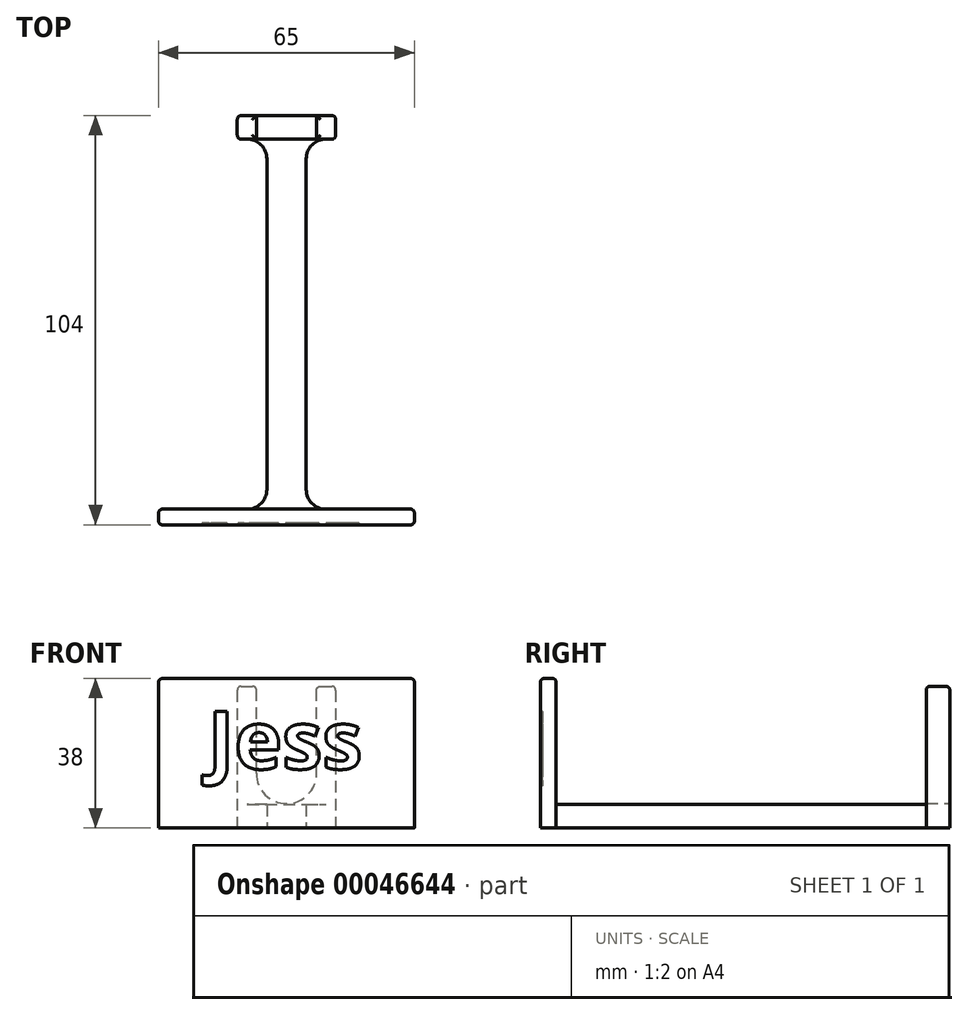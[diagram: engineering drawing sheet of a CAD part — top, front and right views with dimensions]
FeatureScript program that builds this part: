
annotation { "Feature Type Name" : "Feature", "Feature Type Description" : "" }
export const myFeature = defineFeature(function(context is Context, id is Id, definition is map)
    precondition{}
    {
        {
            var Q0;
            Q0=qCreatedBy(makeId("Top.planeOp"),FACE);
            var sketch = newSketch(context, id + "F0", { "sketchPlane" : qUnion([Q0])});
            skLineSegment(sketch, "E0.top", {"start": v(-32.5, -96) * mm, "end": v(32.5, -96) * mm});
            skLineSegment(sketch, "E0.left", {"start": v(-32.5, -92) * mm, "end": v(-32.5, -96) * mm});
            skLineSegment(sketch, "E0.right", {"start": v(32.5, -92) * mm, "end": v(32.5, -96) * mm});
            skLineSegment(sketch, "E1", {"start": v(-5, -92) * mm, "end": v(-5, 2) * mm});
            skLineSegment(sketch, "E2", {"start": v(5, -92) * mm, "end": v(5, 2) * mm});
            skLineSegment(sketch, "E3", {"start": v(32.5, -92) * mm, "end": v(5, -92) * mm});
            skLineSegment(sketch, "E4", {"start": v(-32.5, -92) * mm, "end": v(-5, -92) * mm});
            skLineSegment(sketch, "E5", {"start": v(-12.5, 8) * mm, "end": v(12.5, 8) * mm});
            skLineSegment(sketch, "E6", {"start": v(12.5, 8) * mm, "end": v(12.5, 2) * mm});
            skLineSegment(sketch, "E7", {"start": v(12.5, 2) * mm, "end": v(5, 2) * mm});
            skLineSegment(sketch, "E8", {"start": v(-12.5, 8) * mm, "end": v(-12.5, 2) * mm});
            skLineSegment(sketch, "E9", {"start": v(-12.5, 2) * mm, "end": v(-5, 2) * mm});
            skSolve(sketch);
        }
        {
            var Q0;
            Q0=makeQuery(id+"F0.imprint","IMPRINT",FACE,{"disambiguationData":[TD([[makeQuery(id+"F0.imprint","IMPRINT",EDGE,{"derivedFrom":sQuery(id+"F0.wireOp",EDGE,"E0.top")}),1.0]])]});
            extrude(context, id + "F1", {"entities" : qUnion([Q0]), "depth" : 6 * mm});
        }
        {
            var Q0;
            Q0=makeQuery(id+"F1.opExtrude","CAP_FACE",FACE,{"disambiguationData":[OSD([sQuery(id+"F0.wireOp",EDGE,"E0.top"),sQuery(id+"F0.wireOp",EDGE,"E0.left"),sQuery(id+"F0.wireOp",EDGE,"E0.right"),sQuery(id+"F0.wireOp",EDGE,"E1"),sQuery(id+"F0.wireOp",EDGE,"E2"),sQuery(id+"F0.wireOp",EDGE,"E3"),sQuery(id+"F0.wireOp",EDGE,"E4"),sQuery(id+"F0.wireOp",EDGE,"E5"),sQuery(id+"F0.wireOp",EDGE,"E6"),sQuery(id+"F0.wireOp",EDGE,"E7"),sQuery(id+"F0.wireOp",EDGE,"E8"),sQuery(id+"F0.wireOp",EDGE,"E9")])],"isStart":false});
            var sketch = newSketch(context, id + "F2", { "sketchPlane" : qUnion([Q0])});
            skLineSegment(sketch, "E10.bottom", {"start": v(-32.5, -92) * mm, "end": v(32.5, -92) * mm});
            skLineSegment(sketch, "E10.top", {"start": v(-32.5, -96) * mm, "end": v(32.5, -96) * mm});
            skLineSegment(sketch, "E10.left", {"start": v(-32.5, -92) * mm, "end": v(-32.5, -96) * mm});
            skLineSegment(sketch, "E10.right", {"start": v(32.5, -92) * mm, "end": v(32.5, -96) * mm});
            skSolve(sketch);
        }
        {
            var Q0;
            Q0=makeQuery(id+"F2.imprint","IMPRINT",FACE,{"disambiguationData":[TD([[makeQuery(id+"F2.imprint","IMPRINT",EDGE,{"derivedFrom":sQuery(id+"F2.wireOp",EDGE,"E10.top")}),1.0]])]});
            extrude(context, id + "F3", {"entities" : qUnion([Q0]), "operationType" : NewBodyOperationType.ADD, "depth" : 32 * mm});
        }
        {
            var Q0;
            Q0=makeQuery(id+"F1.opExtrude","CAP_FACE",FACE,{"disambiguationData":[OSD([sQuery(id+"F0.wireOp",EDGE,"E0.top"),sQuery(id+"F0.wireOp",EDGE,"E0.left"),sQuery(id+"F0.wireOp",EDGE,"E0.right"),sQuery(id+"F0.wireOp",EDGE,"E1"),sQuery(id+"F0.wireOp",EDGE,"E2"),sQuery(id+"F0.wireOp",EDGE,"E3"),sQuery(id+"F0.wireOp",EDGE,"E4"),sQuery(id+"F0.wireOp",EDGE,"E5"),sQuery(id+"F0.wireOp",EDGE,"E6"),sQuery(id+"F0.wireOp",EDGE,"E7"),sQuery(id+"F0.wireOp",EDGE,"E8"),sQuery(id+"F0.wireOp",EDGE,"E9")])],"isStart":false});
            var sketch = newSketch(context, id + "F4", { "sketchPlane" : qUnion([Q0])});
            skLineSegment(sketch, "E11.bottom", {"start": v(-12.5, 8) * mm, "end": v(12.5, 8) * mm});
            skLineSegment(sketch, "E11.top", {"start": v(-12.5, 2) * mm, "end": v(12.5, 2) * mm});
            skLineSegment(sketch, "E11.left", {"start": v(-12.5, 8) * mm, "end": v(-12.5, 2) * mm});
            skLineSegment(sketch, "E11.right", {"start": v(12.5, 8) * mm, "end": v(12.5, 2) * mm});
            skSolve(sketch);
        }
        {
            var Q0;
            Q0=makeQuery(id+"F4.imprint","IMPRINT",FACE,{"disambiguationData":[TD([[makeQuery(id+"F4.imprint","IMPRINT",EDGE,{"derivedFrom":sQuery(id+"F4.wireOp",EDGE,"E11.bottom")}),-1.0]])]});
            extrude(context, id + "F5", {"entities" : qUnion([Q0]), "operationType" : NewBodyOperationType.ADD, "depth" : 30 * mm});
        }
        {
            var Q0;
            Q0=makeQuery(id+"F5.boolean.opBoolean","MERGE",FACE,{"derivedFrom":[makeQuery(id+"F1.opExtrude","SWEPT_FACE",FACE,{"disambiguationData":[OSD([sQuery(id+"F0.wireOp",EDGE,"E5")])]}),makeQuery(id+"F5.opExtrude","SWEPT_FACE",FACE,{"disambiguationData":[OSD([sQuery(id+"F4.wireOp",EDGE,"E11.bottom")])]})]});
            var sketch = newSketch(context, id + "F6", { "sketchPlane" : qUnion([Q0])});
            skCircle(sketch, "E12", {"center": v(0, 13.85) * mm, "radius": 7.65 * mm});
            skLineSegment(sketch, "E13", {"start": v(-7.65, 13.85) * mm, "end": v(-7.65, 36) * mm});
            skLineSegment(sketch, "E14", {"start": v(7.65, 13.85) * mm, "end": v(7.65, 36) * mm});
            skLineSegment(sketch, "E15", {"start": v(7.65, 36) * mm, "end": v(-7.65, 36) * mm});
            skSolve(sketch);
        }
        {
            var Q0;
            {var subQ1=sQuery(id+"F6.wireOp",EDGE,"E13");Q0=makeQuery(id+"F6.imprint","IMPRINT",FACE,{"disambiguationData":[TD([[makeQuery(id+"F6.imprint","IMPRINT",EDGE,{"derivedFrom":subQ1}),-1.0]])]});}
            var Q1;
            {var subQ0=sQuery(id+"F6.wireOp",EDGE,"E12");var subQ2=makeQuery(id+"F6.imprint","INTERSECT",VERTEX,{"derivedFrom":[subQ0,sQuery(id+"F6.wireOp",EDGE,"E13")]});Q1=makeQuery(id+"F6.imprint","IMPRINT",FACE,{"disambiguationData":[TD([[makeQuery(id+"F6.imprint","IMPRINT",EDGE,{"disambiguationData":[TD([[subQ2,1.0]])],"derivedFrom":subQ0}),1.0]])]});}
            var Q2;
            Q2=makeQuery(id+"F5.boolean.opBoolean","MERGE",FACE,{"derivedFrom":[makeQuery(id+"F1.opExtrude","SWEPT_FACE",FACE,{"disambiguationData":[OSD([sQuery(id+"F0.wireOp",EDGE,"E7")])]}),makeQuery(id+"F1.opExtrude","SWEPT_FACE",FACE,{"disambiguationData":[OSD([sQuery(id+"F0.wireOp",EDGE,"E9")])]}),makeQuery(id+"F5.opExtrude","SWEPT_FACE",FACE,{"disambiguationData":[OSD([sQuery(id+"F4.wireOp",EDGE,"E11.top")])]})]});
            extrude(context, id + "F7", {"entities" : qUnion([Q0, Q1]), "operationType" : NewBodyOperationType.REMOVE, "endBound" : BoundingType.UP_TO_SURFACE, "oppositeDirection" : true, "endBoundEntityFace" : qUnion([Q2]), "depth" : 25 * mm});
        }
        {
            var Q0;
            Q0=makeQuery(id+"F1.opExtrude","SWEPT_EDGE",EDGE,{"disambiguationData":[OSD([sQuery(id+"F0.wireOp",EDGE,"E1"),sQuery(id+"F0.wireOp",EDGE,"E9")])]});
            var Q1;
            Q1=makeQuery(id+"F1.opExtrude","SWEPT_EDGE",EDGE,{"disambiguationData":[OSD([sQuery(id+"F0.wireOp",EDGE,"E2"),sQuery(id+"F0.wireOp",EDGE,"E7")])]});
            fillet(context, id + "F8", {"entities" : qUnion([Q0, Q1]), "radius" : 5 * mm, "tangentPropagation" : true, "allowEdgeOverflow" : false});
        }
        {
            var Q0;
            Q0=makeQuery(id+"F1.opExtrude","SWEPT_EDGE",EDGE,{"disambiguationData":[OSD([sQuery(id+"F0.wireOp",EDGE,"E1"),sQuery(id+"F0.wireOp",EDGE,"E4")])]});
            var Q1;
            Q1=makeQuery(id+"F3.opExtrude","CAP_EDGE",EDGE,{"disambiguationData":[OSD([sQuery(id+"F2.wireOp",EDGE,"E10.bottom")])],"isStart":true});
            var Q2;
            Q2=makeQuery(id+"F1.opExtrude","SWEPT_EDGE",EDGE,{"disambiguationData":[OSD([sQuery(id+"F0.wireOp",EDGE,"E2"),sQuery(id+"F0.wireOp",EDGE,"E3")])]});
            fillet(context, id + "F9", {"entities" : qUnion([Q0, Q1, Q2]), "radius" : 5 * mm, "tangentPropagation" : true, "allowEdgeOverflow" : false});
        }
        {
            var Q0;
            {var subQ0=sQuery(id+"F4.wireOp",EDGE,"E11.left");var subQ1=sQuery(id+"F4.wireOp",EDGE,"E11.bottom");var subQ2=sQuery(id+"F4.wireOp",EDGE,"E11.top");Q0=makeQuery(id+"F7.boolean.opBoolean","SPLIT",FACE,{"disambiguationData":[TD([makeQuery(id+"F1.opExtrude","SWEPT_FACE",FACE,{"disambiguationData":[OSD([sQuery(id+"F0.wireOp",EDGE,"E8")])]})])],"derivedFrom":makeQuery(id+"F5.opExtrude","CAP_FACE",FACE,{"disambiguationData":[OSD([subQ1,subQ2,subQ0,sQuery(id+"F4.wireOp",EDGE,"E11.right")])],"isStart":false})});}
            var Q1;
            {var subQ0=sQuery(id+"F4.wireOp",EDGE,"E11.bottom");var subQ1=sQuery(id+"F4.wireOp",EDGE,"E11.top");var subQ2=sQuery(id+"F4.wireOp",EDGE,"E11.right");Q1=makeQuery(id+"F7.boolean.opBoolean","SPLIT",FACE,{"disambiguationData":[TD([makeQuery(id+"F1.opExtrude","SWEPT_FACE",FACE,{"disambiguationData":[OSD([sQuery(id+"F0.wireOp",EDGE,"E6")])]})])],"derivedFrom":makeQuery(id+"F5.opExtrude","CAP_FACE",FACE,{"disambiguationData":[OSD([subQ0,subQ1,sQuery(id+"F4.wireOp",EDGE,"E11.left"),subQ2])],"isStart":false})});}
            var Q2;
            Q2=makeQuery(id+"F3.opExtrude","CAP_FACE",FACE,{"disambiguationData":[OSD([sQuery(id+"F2.wireOp",EDGE,"E10.bottom"),sQuery(id+"F2.wireOp",EDGE,"E10.top"),sQuery(id+"F2.wireOp",EDGE,"E10.left"),sQuery(id+"F2.wireOp",EDGE,"E10.right")])],"isStart":false});
            var Q3;
            Q3=makeQuery(id+"F3.boolean.opBoolean","MERGE",EDGE,{"derivedFrom":[makeQuery(id+"F1.opExtrude","SWEPT_EDGE",EDGE,{"disambiguationData":[OSD([sQuery(id+"F0.wireOp",EDGE,"E0.right"),sQuery(id+"F0.wireOp",EDGE,"E3")])]}),makeQuery(id+"F3.opExtrude","SWEPT_EDGE",EDGE,{"disambiguationData":[OSD([sQuery(id+"F2.wireOp",EDGE,"E10.bottom"),sQuery(id+"F2.wireOp",EDGE,"E10.right")])]})]});
            var Q4;
            Q4=makeQuery(id+"F3.boolean.opBoolean","MERGE",EDGE,{"derivedFrom":[makeQuery(id+"F1.opExtrude","SWEPT_EDGE",EDGE,{"disambiguationData":[OSD([sQuery(id+"F0.wireOp",EDGE,"E0.top"),sQuery(id+"F0.wireOp",EDGE,"E0.right")])]}),makeQuery(id+"F3.opExtrude","SWEPT_EDGE",EDGE,{"disambiguationData":[OSD([sQuery(id+"F2.wireOp",EDGE,"E10.top"),sQuery(id+"F2.wireOp",EDGE,"E10.right")])]})]});
            var Q5;
            Q5=makeQuery(id+"F5.boolean.opBoolean","MERGE",EDGE,{"derivedFrom":[makeQuery(id+"F1.opExtrude","SWEPT_EDGE",EDGE,{"disambiguationData":[OSD([sQuery(id+"F0.wireOp",EDGE,"E6"),sQuery(id+"F0.wireOp",EDGE,"E7")])]}),makeQuery(id+"F5.opExtrude","SWEPT_EDGE",EDGE,{"disambiguationData":[OSD([sQuery(id+"F4.wireOp",EDGE,"E11.top"),sQuery(id+"F4.wireOp",EDGE,"E11.right")])]})]});
            var Q6;
            Q6=makeQuery(id+"F5.boolean.opBoolean","MERGE",EDGE,{"derivedFrom":[makeQuery(id+"F1.opExtrude","SWEPT_EDGE",EDGE,{"disambiguationData":[OSD([sQuery(id+"F0.wireOp",EDGE,"E5"),sQuery(id+"F0.wireOp",EDGE,"E6")])]}),makeQuery(id+"F5.opExtrude","SWEPT_EDGE",EDGE,{"disambiguationData":[OSD([sQuery(id+"F4.wireOp",EDGE,"E11.bottom"),sQuery(id+"F4.wireOp",EDGE,"E11.right")])]})]});
            var Q7;
            Q7=makeQuery(id+"F5.boolean.opBoolean","MERGE",EDGE,{"derivedFrom":[makeQuery(id+"F1.opExtrude","SWEPT_EDGE",EDGE,{"disambiguationData":[OSD([sQuery(id+"F0.wireOp",EDGE,"E5"),sQuery(id+"F0.wireOp",EDGE,"E8")])]}),makeQuery(id+"F5.opExtrude","SWEPT_EDGE",EDGE,{"disambiguationData":[OSD([sQuery(id+"F4.wireOp",EDGE,"E11.bottom"),sQuery(id+"F4.wireOp",EDGE,"E11.left")])]})]});
            var Q8;
            Q8=makeQuery(id+"F5.boolean.opBoolean","MERGE",EDGE,{"derivedFrom":[makeQuery(id+"F1.opExtrude","SWEPT_EDGE",EDGE,{"disambiguationData":[OSD([sQuery(id+"F0.wireOp",EDGE,"E8"),sQuery(id+"F0.wireOp",EDGE,"E9")])]}),makeQuery(id+"F5.opExtrude","SWEPT_EDGE",EDGE,{"disambiguationData":[OSD([sQuery(id+"F4.wireOp",EDGE,"E11.top"),sQuery(id+"F4.wireOp",EDGE,"E11.left")])]})]});
            var Q9;
            Q9=makeQuery(id+"F3.boolean.opBoolean","MERGE",EDGE,{"derivedFrom":[makeQuery(id+"F1.opExtrude","SWEPT_EDGE",EDGE,{"disambiguationData":[OSD([sQuery(id+"F0.wireOp",EDGE,"E0.top"),sQuery(id+"F0.wireOp",EDGE,"E0.left")])]}),makeQuery(id+"F3.opExtrude","SWEPT_EDGE",EDGE,{"disambiguationData":[OSD([sQuery(id+"F2.wireOp",EDGE,"E10.top"),sQuery(id+"F2.wireOp",EDGE,"E10.left")])]})]});
            var Q10;
            Q10=makeQuery(id+"F3.boolean.opBoolean","MERGE",EDGE,{"derivedFrom":[makeQuery(id+"F1.opExtrude","SWEPT_EDGE",EDGE,{"disambiguationData":[OSD([sQuery(id+"F0.wireOp",EDGE,"E0.left"),sQuery(id+"F0.wireOp",EDGE,"E4")])]}),makeQuery(id+"F3.opExtrude","SWEPT_EDGE",EDGE,{"disambiguationData":[OSD([sQuery(id+"F2.wireOp",EDGE,"E10.bottom"),sQuery(id+"F2.wireOp",EDGE,"E10.left")])]})]});
            fillet(context, id + "F10", {"entities" : qUnion([Q0, Q1, Q2, Q3, Q4, Q5, Q6, Q7, Q8, Q9, Q10]), "radius" : 1 * mm, "tangentPropagation" : true, "allowEdgeOverflow" : false});
        }
        {
            var Q0;
            Q0=makeQuery(id+"F3.boolean.opBoolean","MERGE",FACE,{"derivedFrom":[makeQuery(id+"F1.opExtrude","SWEPT_FACE",FACE,{"disambiguationData":[OSD([sQuery(id+"F0.wireOp",EDGE,"E0.top")])]}),makeQuery(id+"F3.opExtrude","SWEPT_FACE",FACE,{"disambiguationData":[OSD([sQuery(id+"F2.wireOp",EDGE,"E10.top")])]})]});
            var sketch = newSketch(context, id + "F11", { "sketchPlane" : qUnion([Q0])});
            skText(sketch, "E16", { "text": "Jess", "fontName": "OpenSans-Bold.ttf"});
            const initialGuessF11  = {"E16": [-0.02, 0.015, 1, 0, 0.01475]};
            skSetInitialGuess(sketch, initialGuessF11);
            skSolve(sketch);
        }
        {
            var Q0;
            Q0 = qSketchRegion(id + "F11", true);
            extrude(context, id + "F12", {"entities" : qUnion([Q0]), "operationType" : NewBodyOperationType.REMOVE, "oppositeDirection" : true, "depth" : 0.5 * mm});
        }
    });
